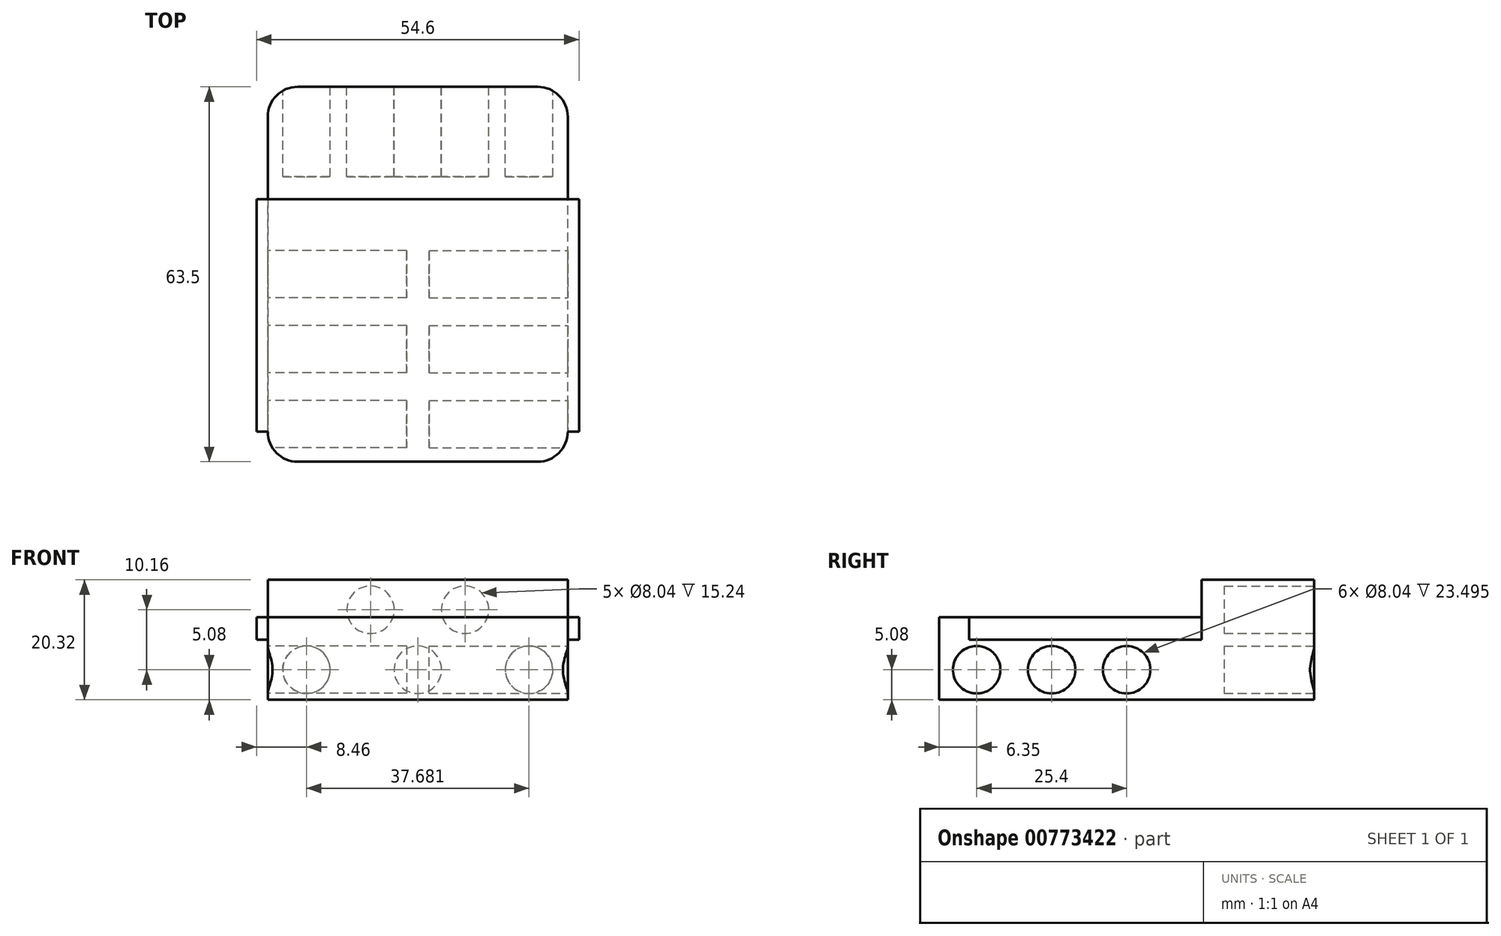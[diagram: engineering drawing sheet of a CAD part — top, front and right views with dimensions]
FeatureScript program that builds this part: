
annotation { "Feature Type Name" : "Feature", "Feature Type Description" : "" }
export const myFeature = defineFeature(function(context is Context, id is Id, definition is map)
    precondition{}
    {
        {
            var Q0;
            Q0=qCreatedBy(makeId("Top.planeOp"),FACE);
            var sketch = newSketch(context, id + "F0", { "sketchPlane" : qUnion([Q0])});
            skLineSegment(sketch, "E0.bottom", {"start": v(25.4, -19.05) * mm, "end": v(-25.4, -19.05) * mm});
            skLineSegment(sketch, "E0.top", {"start": v(25.4, 19.05) * mm, "end": v(-25.4, 19.05) * mm});
            skLineSegment(sketch, "E0.left", {"start": v(25.4, -19.05) * mm, "end": v(25.4, 19.05) * mm});
            skLineSegment(sketch, "E0.right", {"start": v(-25.4, -19.05) * mm, "end": v(-25.4, 19.05) * mm});
            skPoint(sketch, "E0.middle", {"position": v(0, 0) * mm});
            skSolve(sketch);
        }
        {
            var Q0;
            Q0=makeQuery(id+"F0.imprint","IMPRINT",FACE,{"disambiguationData":[TD([[makeQuery(id+"F0.imprint","IMPRINT",EDGE,{"derivedFrom":sQuery(id+"F0.wireOp",EDGE,"E0.bottom")}),-1.0]])]});
            extrude(context, id + "F1", {"entities" : qUnion([Q0]), "depth" : 10.16 * mm});
        }
        {
            var Q0;
            Q0=makeQuery(id+"F1.opExtrude","SWEPT_FACE",FACE,{"disambiguationData":[OSD([sQuery(id+"F0.wireOp",EDGE,"E0.right")])]});
            var sketch = newSketch(context, id + "F2", { "sketchPlane" : qUnion([Q0])});
            skCircle(sketch, "E1", {"center": v(-12.7, 5.08) * mm, "radius": 4.02 * mm});
            skCircle(sketch, "E2", {"center": v(0, 5.08) * mm, "radius": 4.02 * mm});
            skCircle(sketch, "E3", {"center": v(12.7, 5.08) * mm, "radius": 4.02 * mm});
            skSolve(sketch);
        }
        {
            var Q0;
            Q0=makeQuery(id+"F2.imprint","IMPRINT",FACE,{"disambiguationData":[TD([[makeQuery(id+"F2.imprint","IMPRINT",EDGE,{"derivedFrom":sQuery(id+"F2.wireOp",EDGE,"E1")}),1.0]])]});
            var Q1;
            Q1=makeQuery(id+"F2.imprint","IMPRINT",FACE,{"disambiguationData":[TD([[makeQuery(id+"F2.imprint","IMPRINT",EDGE,{"derivedFrom":sQuery(id+"F2.wireOp",EDGE,"E2")}),1.0]])]});
            var Q2;
            Q2=makeQuery(id+"F2.imprint","IMPRINT",FACE,{"disambiguationData":[TD([[makeQuery(id+"F2.imprint","IMPRINT",EDGE,{"derivedFrom":sQuery(id+"F2.wireOp",EDGE,"E3")}),1.0]])]});
            extrude(context, id + "F3", {"entities" : qUnion([Q0, Q1, Q2]), "operationType" : NewBodyOperationType.REMOVE, "oppositeDirection" : true, "depth" : 23.5 * mm});
        }
        {
            var Q0;
            Q0=makeQuery(id+"F1.opExtrude","SWEPT_FACE",FACE,{"disambiguationData":[OSD([sQuery(id+"F0.wireOp",EDGE,"E0.left")])]});
            var sketch = newSketch(context, id + "F4", { "sketchPlane" : qUnion([Q0])});
            skCircle(sketch, "E4", {"center": v(-12.7, 5.08) * mm, "radius": 4.02 * mm});
            skCircle(sketch, "E5", {"center": v(0, 5.08) * mm, "radius": 4.02 * mm});
            skCircle(sketch, "E6", {"center": v(12.7, 5.08) * mm, "radius": 4.02 * mm});
            skSolve(sketch);
        }
        {
            var Q0;
            Q0=makeQuery(id+"F4.imprint","IMPRINT",FACE,{"disambiguationData":[TD([[makeQuery(id+"F4.imprint","IMPRINT",EDGE,{"derivedFrom":sQuery(id+"F4.wireOp",EDGE,"E4")}),1.0]])]});
            var Q1;
            Q1=makeQuery(id+"F4.imprint","IMPRINT",FACE,{"disambiguationData":[TD([[makeQuery(id+"F4.imprint","IMPRINT",EDGE,{"derivedFrom":sQuery(id+"F4.wireOp",EDGE,"E5")}),1.0]])]});
            var Q2;
            Q2=makeQuery(id+"F4.imprint","IMPRINT",FACE,{"disambiguationData":[TD([[makeQuery(id+"F4.imprint","IMPRINT",EDGE,{"derivedFrom":sQuery(id+"F4.wireOp",EDGE,"E6")}),1.0]])]});
            extrude(context, id + "F5", {"entities" : qUnion([Q0, Q1, Q2]), "operationType" : NewBodyOperationType.REMOVE, "oppositeDirection" : true, "depth" : 23.5 * mm});
        }
        {
            var Q0;
            Q0=makeQuery(id+"F1.opExtrude","SWEPT_FACE",FACE,{"disambiguationData":[OSD([sQuery(id+"F0.wireOp",EDGE,"E0.top")])]});
            extrude(context, id + "F6", {"entities" : qUnion([Q0]), "operationType" : NewBodyOperationType.ADD, "depth" : 25.4 * mm});
        }
        {
            var Q0;
            {var subQ0=sQuery(id+"F0.wireOp",EDGE,"E0.top");Q0=makeQuery(id+"F6.boolean.opBoolean","MERGE",FACE,{"derivedFrom":[makeQuery(id+"F1.opExtrude","CAP_FACE",FACE,{"disambiguationData":[OSD([sQuery(id+"F0.wireOp",EDGE,"E0.bottom"),subQ0,sQuery(id+"F0.wireOp",EDGE,"E0.left"),sQuery(id+"F0.wireOp",EDGE,"E0.right")])],"isStart":false}),makeQuery(id+"F6.opExtrude","SWEPT_FACE",FACE,{"disambiguationData":[OSD([subQ0]),TDD([makeQuery(id+"F1.opExtrude","CAP_EDGE",EDGE,{"disambiguationData":[OSD([subQ0])],"isStart":false})])]})]});}
            var sketch = newSketch(context, id + "F7", { "sketchPlane" : qUnion([Q0])});
            skLineSegment(sketch, "E7.bottom", {"start": v(25.4, 44.45) * mm, "end": v(-25.4, 44.45) * mm});
            skLineSegment(sketch, "E7.top", {"start": v(25.4, 25.4) * mm, "end": v(-25.4, 25.4) * mm});
            skLineSegment(sketch, "E7.left", {"start": v(25.4, 44.45) * mm, "end": v(25.4, 25.4) * mm});
            skLineSegment(sketch, "E7.right", {"start": v(-25.4, 44.45) * mm, "end": v(-25.4, 25.4) * mm});
            skSolve(sketch);
        }
        {
            var Q0;
            Q0=makeQuery(id+"F7.imprint","IMPRINT",FACE,{"disambiguationData":[TD([[makeQuery(id+"F7.imprint","IMPRINT",EDGE,{"derivedFrom":sQuery(id+"F7.wireOp",EDGE,"E7.bottom")}),1.0]])]});
            extrude(context, id + "F8", {"entities" : qUnion([Q0]), "operationType" : NewBodyOperationType.ADD, "depth" : 10.16 * mm});
        }
        {
            var Q0;
            Q0=makeQuery(id+"F8.boolean.opBoolean","MERGE",FACE,{"derivedFrom":[makeQuery(id+"F6.opExtrude","CAP_FACE",FACE,{"disambiguationData":[OSD([sQuery(id+"F0.wireOp",EDGE,"E0.top")])],"isStart":false}),makeQuery(id+"F8.opExtrude","SWEPT_FACE",FACE,{"disambiguationData":[OSD([sQuery(id+"F7.wireOp",EDGE,"E7.bottom")])]})]});
            var sketch = newSketch(context, id + "F9", { "sketchPlane" : qUnion([Q0])});
            skCircle(sketch, "E8", {"center": v(-8, 15.24) * mm, "radius": 4.02 * mm});
            skCircle(sketch, "E9", {"center": v(8, 15.24) * mm, "radius": 4.02 * mm});
            skCircle(sketch, "E10", {"center": v(-18.84, 5.08) * mm, "radius": 4.02 * mm});
            skCircle(sketch, "E11", {"center": v(0, 5.08) * mm, "radius": 4.02 * mm});
            skCircle(sketch, "E12", {"center": v(18.84, 5.08) * mm, "radius": 4.02 * mm});
            skSolve(sketch);
        }
        {
            var Q0;
            Q0=makeQuery(id+"F9.imprint","IMPRINT",FACE,{"disambiguationData":[TD([[makeQuery(id+"F9.imprint","IMPRINT",EDGE,{"derivedFrom":sQuery(id+"F9.wireOp",EDGE,"E11")}),1.0]])]});
            var Q1;
            Q1=makeQuery(id+"F9.imprint","IMPRINT",FACE,{"disambiguationData":[TD([[makeQuery(id+"F9.imprint","IMPRINT",EDGE,{"derivedFrom":sQuery(id+"F9.wireOp",EDGE,"E8")}),1.0]])]});
            var Q2;
            Q2=makeQuery(id+"F9.imprint","IMPRINT",FACE,{"disambiguationData":[TD([[makeQuery(id+"F9.imprint","IMPRINT",EDGE,{"derivedFrom":sQuery(id+"F9.wireOp",EDGE,"E10")}),1.0]])]});
            var Q3;
            Q3=makeQuery(id+"F9.imprint","IMPRINT",FACE,{"disambiguationData":[TD([[makeQuery(id+"F9.imprint","IMPRINT",EDGE,{"derivedFrom":sQuery(id+"F9.wireOp",EDGE,"E9")}),1.0]])]});
            var Q4;
            Q4=makeQuery(id+"F9.imprint","IMPRINT",FACE,{"disambiguationData":[TD([[makeQuery(id+"F9.imprint","IMPRINT",EDGE,{"derivedFrom":sQuery(id+"F9.wireOp",EDGE,"E12")}),1.0]])]});
            extrude(context, id + "F10", {"entities" : qUnion([Q0, Q1, Q2, Q3, Q4]), "operationType" : NewBodyOperationType.REMOVE, "oppositeDirection" : true, "depth" : 15.24 * mm});
        }
        {
            var Q0;
            Q0=makeQuery(id+"F1.opExtrude","SWEPT_EDGE",EDGE,{"disambiguationData":[OSD([sQuery(id+"F0.wireOp",EDGE,"E0.bottom"),sQuery(id+"F0.wireOp",EDGE,"E0.right")])]});
            var Q1;
            Q1=makeQuery(id+"F1.opExtrude","SWEPT_EDGE",EDGE,{"disambiguationData":[OSD([sQuery(id+"F0.wireOp",EDGE,"E0.bottom"),sQuery(id+"F0.wireOp",EDGE,"E0.left")])]});
            fillet(context, id + "F11", {"entities" : qUnion([Q0, Q1]), "radius" : 5.08 * mm, "tangentPropagation" : true, "allowEdgeOverflow" : false});
        }
        {
            var Q0;
            Q0=makeQuery(id+"F8.boolean.opBoolean","MERGE",EDGE,{"derivedFrom":[makeQuery(id+"F6.opExtrude","CAP_EDGE",EDGE,{"disambiguationData":[OSD([sQuery(id+"F0.wireOp",EDGE,"E0.top"),sQuery(id+"F0.wireOp",EDGE,"E0.right")])],"isStart":false}),makeQuery(id+"F8.opExtrude","SWEPT_EDGE",EDGE,{"disambiguationData":[OSD([sQuery(id+"F7.wireOp",EDGE,"E7.bottom"),sQuery(id+"F7.wireOp",EDGE,"E7.right")])]})]});
            var Q1;
            Q1=makeQuery(id+"F8.boolean.opBoolean","MERGE",EDGE,{"derivedFrom":[makeQuery(id+"F6.opExtrude","CAP_EDGE",EDGE,{"disambiguationData":[OSD([sQuery(id+"F0.wireOp",EDGE,"E0.top"),sQuery(id+"F0.wireOp",EDGE,"E0.left")])],"isStart":false}),makeQuery(id+"F8.opExtrude","SWEPT_EDGE",EDGE,{"disambiguationData":[OSD([sQuery(id+"F7.wireOp",EDGE,"E7.bottom"),sQuery(id+"F7.wireOp",EDGE,"E7.left")])]})]});
            fillet(context, id + "F12", {"entities" : qUnion([Q0, Q1]), "radius" : 5.08 * mm, "tangentPropagation" : true, "allowEdgeOverflow" : false});
        }
        {
            var Q0;
            {var subQ0=sQuery(id+"F0.wireOp",EDGE,"E0.top");Q0=makeQuery(id+"F6.boolean.opBoolean","MERGE",FACE,{"derivedFrom":[makeQuery(id+"F1.opExtrude","CAP_FACE",FACE,{"disambiguationData":[OSD([sQuery(id+"F0.wireOp",EDGE,"E0.bottom"),subQ0,sQuery(id+"F0.wireOp",EDGE,"E0.left"),sQuery(id+"F0.wireOp",EDGE,"E0.right")])],"isStart":false}),makeQuery(id+"F6.opExtrude","SWEPT_FACE",FACE,{"disambiguationData":[OSD([subQ0]),TDD([makeQuery(id+"F1.opExtrude","CAP_EDGE",EDGE,{"disambiguationData":[OSD([subQ0])],"isStart":false})])]})]});}
            extrude(context, id + "F13", {"entities" : qUnion([Q0]), "operationType" : NewBodyOperationType.ADD, "depth" : 3.8 * mm});
        }
        {
            var Q0;
            {var subQ0=sQuery(id+"F0.wireOp",EDGE,"E0.left");var subQ1=sQuery(id+"F0.wireOp",EDGE,"E0.top");Q0=makeQuery(id+"F13.boolean.opBoolean","MERGE",FACE,{"derivedFrom":[makeQuery(id+"F8.boolean.opBoolean","MERGE",FACE,{"derivedFrom":[makeQuery(id+"F6.boolean.opBoolean","MERGE",FACE,{"derivedFrom":[makeQuery(id+"F1.opExtrude","SWEPT_FACE",FACE,{"disambiguationData":[OSD([subQ0])]}),makeQuery(id+"F6.opExtrude","SWEPT_FACE",FACE,{"disambiguationData":[OSD([subQ1,subQ0])]})]}),makeQuery(id+"F8.opExtrude","SWEPT_FACE",FACE,{"disambiguationData":[OSD([sQuery(id+"F7.wireOp",EDGE,"E7.left")])]})]}),makeQuery(id+"F13.opExtrude","SWEPT_FACE",FACE,{"disambiguationData":[OSD([subQ1,subQ0])]})]});}
            var sketch = newSketch(context, id + "F14", { "sketchPlane" : qUnion([Q0])});
            skLineSegment(sketch, "E13.bottom", {"start": v(-13.97, 13.97) * mm, "end": v(25.4, 13.97) * mm});
            skLineSegment(sketch, "E13.top", {"start": v(-13.97, 10.16) * mm, "end": v(25.4, 10.16) * mm});
            skLineSegment(sketch, "E13.left", {"start": v(-13.97, 13.97) * mm, "end": v(-13.97, 10.16) * mm});
            skLineSegment(sketch, "E13.right", {"start": v(25.4, 13.97) * mm, "end": v(25.4, 10.16) * mm});
            skSolve(sketch);
        }
        {
            var Q0;
            {var subQ0=sQuery(id+"F0.wireOp",EDGE,"E0.right");var subQ1=sQuery(id+"F0.wireOp",EDGE,"E0.top");Q0=makeQuery(id+"F13.boolean.opBoolean","MERGE",FACE,{"derivedFrom":[makeQuery(id+"F8.boolean.opBoolean","MERGE",FACE,{"derivedFrom":[makeQuery(id+"F6.boolean.opBoolean","MERGE",FACE,{"derivedFrom":[makeQuery(id+"F1.opExtrude","SWEPT_FACE",FACE,{"disambiguationData":[OSD([subQ0])]}),makeQuery(id+"F6.opExtrude","SWEPT_FACE",FACE,{"disambiguationData":[OSD([subQ1,subQ0])]})]}),makeQuery(id+"F8.opExtrude","SWEPT_FACE",FACE,{"disambiguationData":[OSD([sQuery(id+"F7.wireOp",EDGE,"E7.right")])]})]}),makeQuery(id+"F13.opExtrude","SWEPT_FACE",FACE,{"disambiguationData":[OSD([subQ1,subQ0])]})]});}
            var sketch = newSketch(context, id + "F15", { "sketchPlane" : qUnion([Q0])});
            skLineSegment(sketch, "E14.bottom", {"start": v(-25.4, 13.97) * mm, "end": v(13.97, 13.97) * mm});
            skLineSegment(sketch, "E14.top", {"start": v(-25.4, 10.16) * mm, "end": v(13.97, 10.16) * mm});
            skLineSegment(sketch, "E14.left", {"start": v(-25.4, 13.97) * mm, "end": v(-25.4, 10.16) * mm});
            skLineSegment(sketch, "E14.right", {"start": v(13.97, 13.97) * mm, "end": v(13.97, 10.16) * mm});
            skSolve(sketch);
        }
        {
            var Q0;
            Q0=makeQuery(id+"F15.imprint","IMPRINT",FACE,{"disambiguationData":[TD([[makeQuery(id+"F15.imprint","IMPRINT",EDGE,{"derivedFrom":sQuery(id+"F15.wireOp",EDGE,"E14.bottom")}),1.0]])]});
            extrude(context, id + "F16", {"entities" : qUnion([Q0]), "operationType" : NewBodyOperationType.ADD, "depth" : 1.9 * mm});
        }
        {
            var Q0;
            Q0=makeQuery(id+"F14.imprint","IMPRINT",FACE,{"disambiguationData":[TD([[makeQuery(id+"F14.imprint","IMPRINT",EDGE,{"derivedFrom":sQuery(id+"F14.wireOp",EDGE,"E13.bottom")}),-1.0]])]});
            extrude(context, id + "F17", {"entities" : qUnion([Q0]), "operationType" : NewBodyOperationType.ADD, "depth" : 1.9 * mm});
        }
    });
